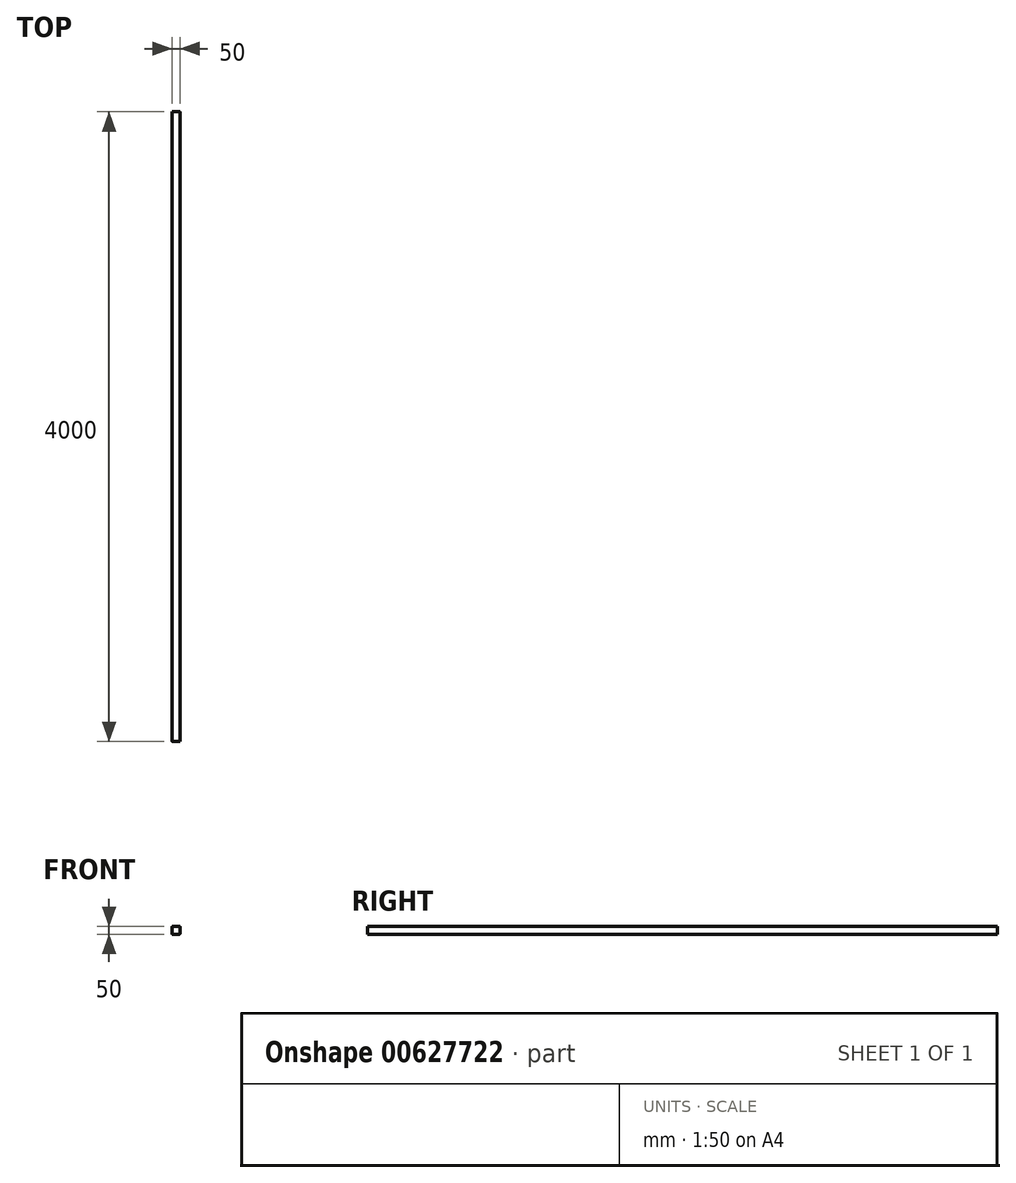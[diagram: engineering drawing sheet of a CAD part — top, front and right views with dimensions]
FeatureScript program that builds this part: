
annotation { "Feature Type Name" : "Feature", "Feature Type Description" : "" }
export const myFeature = defineFeature(function(context is Context, id is Id, definition is map)
    precondition{}
    {
        {
            var Q0;
            Q0=qCreatedBy(makeId("Front.planeOp"),FACE);
            var sketch = newSketch(context, id + "F0", { "sketchPlane" : qUnion([Q0])});
            skLineSegment(sketch, "E0.bottom", {"start": v(0.67, -18.87) * mm, "end": v(44.67, -18.87) * mm});
            skLineSegment(sketch, "E0.top", {"start": v(0.67, 31.13) * mm, "end": v(44.67, 31.13) * mm});
            skLineSegment(sketch, "E0.left", {"start": v(-2.33, -15.87) * mm, "end": v(-2.33, 28.13) * mm});
            skLineSegment(sketch, "E0.right", {"start": v(47.67, -15.87) * mm, "end": v(47.67, 28.13) * mm});
            skPoint(sketch, "E1.visualSharp", {"position": v(-2.33, 31.13) * mm});
            skArc(sketch, "E1.filletArc", {"start": v(0.67, 31.13) * mm, "mid": v(-1.46, 30.26) * mm, "end": v(-2.33, 28.13) * mm});
            skPoint(sketch, "E2.visualSharp", {"position": v(47.67, 31.13) * mm});
            skArc(sketch, "E2.filletArc", {"start": v(47.67, 28.13) * mm, "mid": v(46.79, 30.26) * mm, "end": v(44.67, 31.13) * mm});
            skPoint(sketch, "E3.visualSharp", {"position": v(47.67, -18.87) * mm});
            skArc(sketch, "E3.filletArc", {"start": v(44.67, -18.87) * mm, "mid": v(46.79, -17.99) * mm, "end": v(47.67, -15.87) * mm});
            skPoint(sketch, "E4.visualSharp", {"position": v(-2.33, -18.87) * mm});
            skArc(sketch, "E4.filletArc", {"start": v(-2.33, -15.87) * mm, "mid": v(-1.46, -17.99) * mm, "end": v(0.67, -18.87) * mm});
            skSolve(sketch);
        }
        {
            var Q0;
            Q0 = qSketchRegion(id + "F0", true);
            extrude(context, id + "F1", {"entities" : qUnion([Q0]), "depth" : 4000 * mm, "offsetDistance" : 25 * mm});
        }
    });
